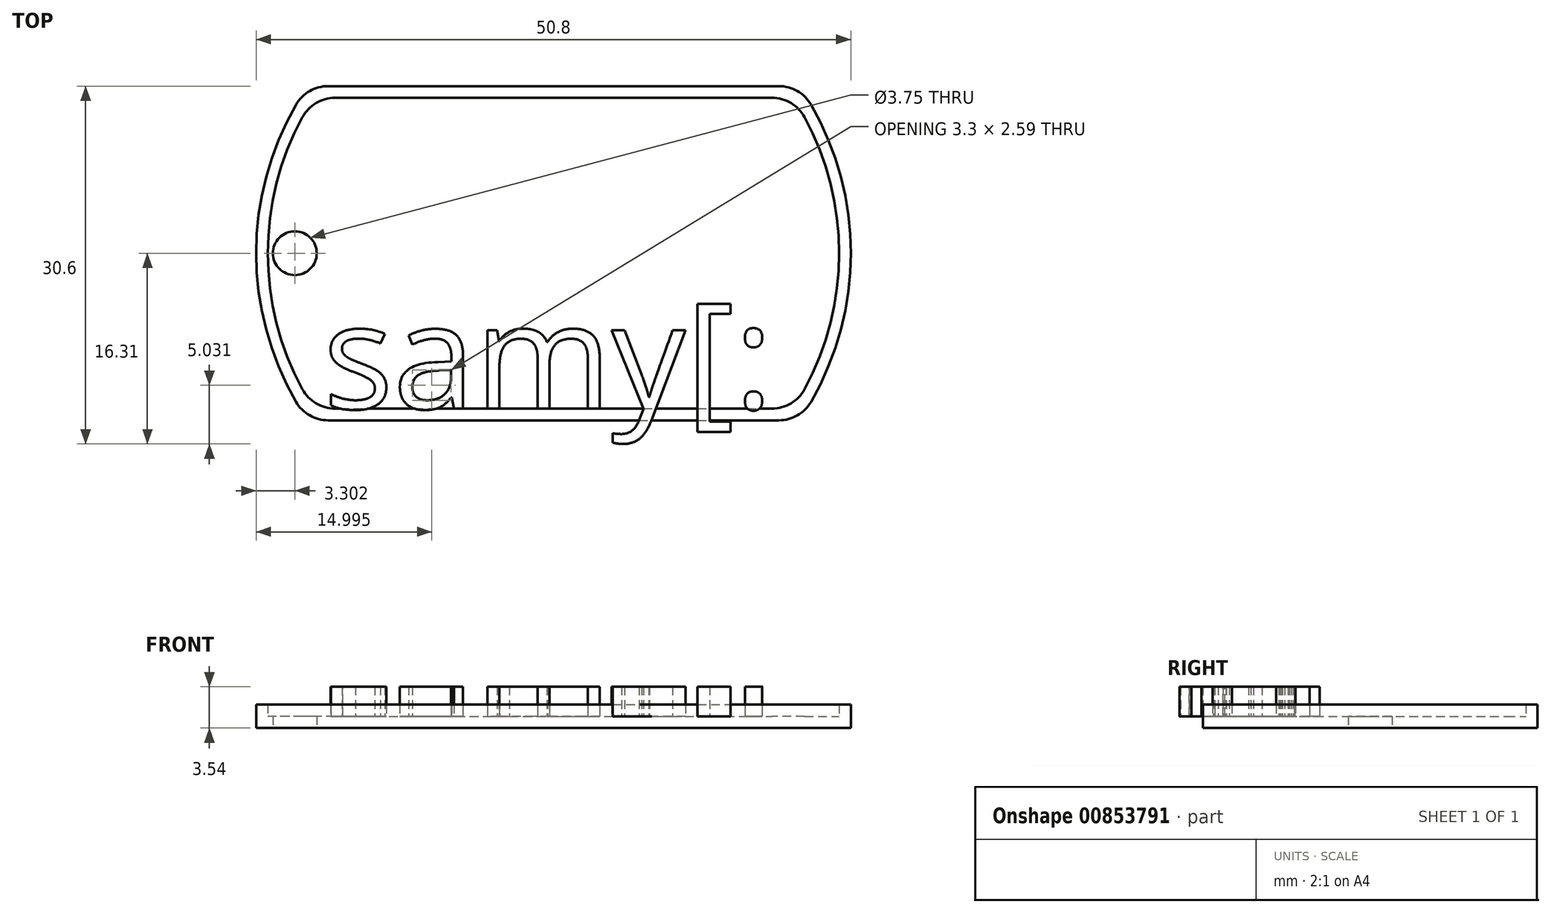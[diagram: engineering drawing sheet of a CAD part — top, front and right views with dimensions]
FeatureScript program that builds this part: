
annotation { "Feature Type Name" : "Feature", "Feature Type Description" : "" }
export const myFeature = defineFeature(function(context is Context, id is Id, definition is map)
    precondition{}
    {
        {
            var Q0;
            Q0=qCreatedBy(makeId("Top.planeOp"),FACE);
            var sketch = newSketch(context, id + "F0", { "sketchPlane" : qUnion([Q0])});
            skArc(sketch, "E0", {"start": v(-22, 12.7) * mm, "mid": v(-25.4, 0) * mm, "end": v(-22, -12.7) * mm});
            skLineSegment(sketch, "E1.top", {"start": v(-19.25, -14.29) * mm, "end": v(19.25, -14.29) * mm});
            skArc(sketch, "E2.trimOffspring", {"start": v(22, -12.7) * mm, "mid": v(25.4, 0) * mm, "end": v(22, 12.7) * mm});
            skLineSegment(sketch, "E3", {"start": v(-19.25, 14.29) * mm, "end": v(19.25, 14.29) * mm});
            skPoint(sketch, "E4.visualSharp", {"position": v(-21, 14.29) * mm});
            skArc(sketch, "E4.filletArc", {"start": v(-19.25, 14.29) * mm, "mid": v(-20.83, 13.86) * mm, "end": v(-22, 12.7) * mm});
            skPoint(sketch, "E5.visualSharp", {"position": v(21, 14.29) * mm});
            skArc(sketch, "E5.filletArc", {"start": v(22, 12.7) * mm, "mid": v(20.83, 13.86) * mm, "end": v(19.25, 14.29) * mm});
            skPoint(sketch, "E6.visualSharp", {"position": v(21, -14.29) * mm});
            skArc(sketch, "E6.filletArc", {"start": v(19.25, -14.29) * mm, "mid": v(20.83, -13.86) * mm, "end": v(22, -12.7) * mm});
            skPoint(sketch, "E7.visualSharp", {"position": v(-21, -14.29) * mm});
            skArc(sketch, "E7.filletArc", {"start": v(-22, -12.7) * mm, "mid": v(-20.83, -13.86) * mm, "end": v(-19.25, -14.29) * mm});
            skCircle(sketch, "E8", {"center": v(-22.1, 0) * mm, "radius": 1.87 * mm});
            skSolve(sketch);
        }
        {
            var Q0;
            Q0=makeQuery(id+"F0.imprint","IMPRINT",FACE,{"disambiguationData":[TD([[makeQuery(id+"F0.imprint","IMPRINT",EDGE,{"derivedFrom":sQuery(id+"F0.wireOp",EDGE,"E0")}),1.0]])]});
            extrude(context, id + "F1", {"entities" : qUnion([Q0]), "depth" : 1 * mm, "offsetDistance" : 25.4 * mm});
        }
        {
            var Q0;
            Q0=makeQuery(id+"F1.opExtrude","CAP_FACE",FACE,{"disambiguationData":[OSD([sQuery(id+"F0.wireOp",EDGE,"E0"),sQuery(id+"F0.wireOp",EDGE,"E1.top"),sQuery(id+"F0.wireOp",EDGE,"E2.trimOffspring"),sQuery(id+"F0.wireOp",EDGE,"E3"),sQuery(id+"F0.wireOp",EDGE,"E4.filletArc"),sQuery(id+"F0.wireOp",EDGE,"E5.filletArc"),sQuery(id+"F0.wireOp",EDGE,"E6.filletArc"),sQuery(id+"F0.wireOp",EDGE,"E7.filletArc")])],"isStart":false});
            var sketch = newSketch(context, id + "F2", { "sketchPlane" : qUnion([Q0])});
            skLineSegment(sketch, "E9.0", {"start": v(-18.66, 13.29) * mm, "end": v(18.66, 13.29) * mm});
            skArc(sketch, "E9.1", {"start": v(-21.45, 11.63) * mm, "mid": v(-24.4, 0) * mm, "end": v(-21.45, -11.63) * mm});
            skLineSegment(sketch, "E9.2", {"start": v(-18.66, -13.29) * mm, "end": v(18.66, -13.29) * mm});
            skArc(sketch, "E9.3", {"start": v(21.45, -11.63) * mm, "mid": v(24.4, 0) * mm, "end": v(21.45, 11.63) * mm});
            skPoint(sketch, "E10.visualSharp", {"position": v(-20.46, 13.29) * mm});
            skArc(sketch, "E10.filletArc", {"start": v(-18.66, 13.29) * mm, "mid": v(-20.29, 12.84) * mm, "end": v(-21.45, 11.63) * mm});
            skPoint(sketch, "E11.visualSharp", {"position": v(20.46, 13.29) * mm});
            skArc(sketch, "E11.filletArc", {"start": v(21.45, 11.63) * mm, "mid": v(20.29, 12.84) * mm, "end": v(18.66, 13.29) * mm});
            skPoint(sketch, "E12.visualSharp", {"position": v(20.46, -13.29) * mm});
            skArc(sketch, "E12.filletArc", {"start": v(18.66, -13.29) * mm, "mid": v(20.29, -12.84) * mm, "end": v(21.45, -11.63) * mm});
            skPoint(sketch, "E13.visualSharp", {"position": v(-20.46, -13.29) * mm});
            skArc(sketch, "E13.filletArc", {"start": v(-21.45, -11.63) * mm, "mid": v(-20.29, -12.84) * mm, "end": v(-18.66, -13.29) * mm});
            skLineSegment(sketch, "E14.0", {"start": v(-19.25, 14.29) * mm, "end": v(19.25, 14.29) * mm});
            skArc(sketch, "E14.1", {"start": v(-22, 12.7) * mm, "mid": v(-25.4, 0) * mm, "end": v(-22, -12.7) * mm});
            skLineSegment(sketch, "E14.2", {"start": v(-19.25, -14.29) * mm, "end": v(19.25, -14.29) * mm});
            skArc(sketch, "E14.3", {"start": v(22, -12.7) * mm, "mid": v(25.4, 0) * mm, "end": v(22, 12.7) * mm});
            skPoint(sketch, "E15.visualSharp", {"position": v(-21, -14.29) * mm});
            skArc(sketch, "E15.filletArc", {"start": v(-22, -12.7) * mm, "mid": v(-20.83, -13.86) * mm, "end": v(-19.25, -14.29) * mm});
            skPoint(sketch, "E16.visualSharp", {"position": v(21, -14.29) * mm});
            skArc(sketch, "E16.filletArc", {"start": v(19.25, -14.29) * mm, "mid": v(20.83, -13.86) * mm, "end": v(22, -12.7) * mm});
            skPoint(sketch, "E17.visualSharp", {"position": v(21, 14.29) * mm});
            skArc(sketch, "E17.filletArc", {"start": v(22, 12.7) * mm, "mid": v(20.83, 13.86) * mm, "end": v(19.25, 14.29) * mm});
            skPoint(sketch, "E18.visualSharp", {"position": v(-21, 14.29) * mm});
            skArc(sketch, "E18.filletArc", {"start": v(-19.25, 14.29) * mm, "mid": v(-20.83, 13.86) * mm, "end": v(-22, 12.7) * mm});
            skSolve(sketch);
        }
        {
            var Q0;
            Q0=makeQuery(id+"F2.imprint","IMPRINT",FACE,{"disambiguationData":[TD([[makeQuery(id+"F2.imprint","IMPRINT",EDGE,{"derivedFrom":sQuery(id+"F2.wireOp",EDGE,"E9.0")}),1.0]])]});
            extrude(context, id + "F3", {"entities" : qUnion([Q0]), "operationType" : NewBodyOperationType.ADD, "depth" : 1 * mm, "offsetDistance" : 25.4 * mm});
        }
        {
            var Q0;
            Q0=makeQuery(id+"F1.opExtrude","CAP_FACE",FACE,{"disambiguationData":[OSD([sQuery(id+"F0.wireOp",EDGE,"E0"),sQuery(id+"F0.wireOp",EDGE,"E1.top"),sQuery(id+"F0.wireOp",EDGE,"E2.trimOffspring"),sQuery(id+"F0.wireOp",EDGE,"E3"),sQuery(id+"F0.wireOp",EDGE,"E4.filletArc"),sQuery(id+"F0.wireOp",EDGE,"E5.filletArc"),sQuery(id+"F0.wireOp",EDGE,"E6.filletArc"),sQuery(id+"F0.wireOp",EDGE,"E7.filletArc"),sQuery(id+"F0.wireOp",EDGE,"E8")])],"isStart":false});
            var sketch = newSketch(context, id + "F4", { "sketchPlane" : qUnion([Q0])});
            skText(sketch, "E19", { "text": "samy[:", "fontName": "OpenSans-Regular.ttf"});
            const initialGuessF4  = {"E19": [-0.01969, -0.01329, 1, 0, 0.00904]};
            skSetInitialGuess(sketch, initialGuessF4);
            skSolve(sketch);
        }
        {
            var Q0;
            Q0 = qSketchRegion(id + "F4", true);
            extrude(context, id + "F5", {"entities" : qUnion([Q0]), "depth" : 2.54 * mm, "offsetDistance" : 25.4 * mm});
        }
    });
